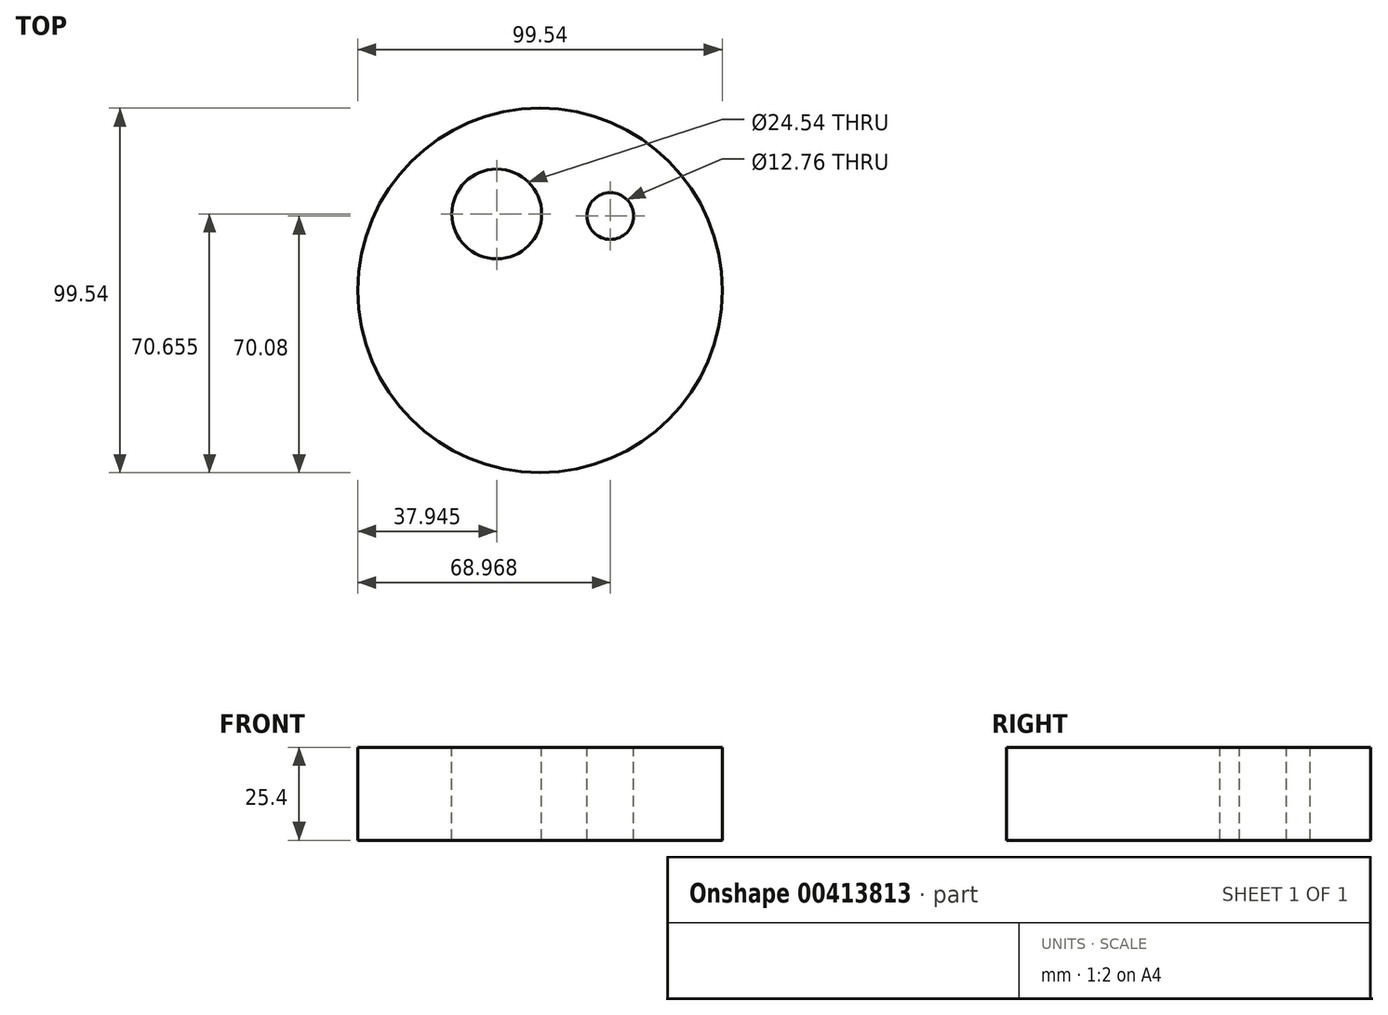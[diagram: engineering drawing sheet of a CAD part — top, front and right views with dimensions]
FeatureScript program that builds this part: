
annotation { "Feature Type Name" : "Feature", "Feature Type Description" : "" }
export const myFeature = defineFeature(function(context is Context, id is Id, definition is map)
    precondition{}
    {
        {
            var Q0;
            Q0=qCreatedBy(makeId("Top.planeOp"),FACE);
            var sketch = newSketch(context, id + "F0", { "sketchPlane" : qUnion([Q0])});
            skCircle(sketch, "E0", {"center": v(0, 0) * mm, "radius": 49.77 * mm});
            skArc(sketch, "E1", {"start": v(-20.16, 0) * mm, "mid": v(0, -20.16) * mm, "end": v(20.16, 0) * mm});
            skCircle(sketch, "E2", {"center": v(-11.83, 20.88) * mm, "radius": 12.27 * mm});
            skCircle(sketch, "E3", {"center": v(19.2, 20.31) * mm, "radius": 6.38 * mm});
            skSolve(sketch);
        }
        {
            var Q0;
            Q0=makeQuery(id+"F0.imprint","IMPRINT",FACE,{"disambiguationData":[TD([[makeQuery(id+"F0.imprint","IMPRINT",EDGE,{"derivedFrom":sQuery(id+"F0.wireOp",EDGE,"E0")}),1.0]])]});
            extrude(context, id + "F1", {"entities" : qUnion([Q0]), "oppositeDirection" : true, "depth" : 25.4 * mm});
        }
    });
